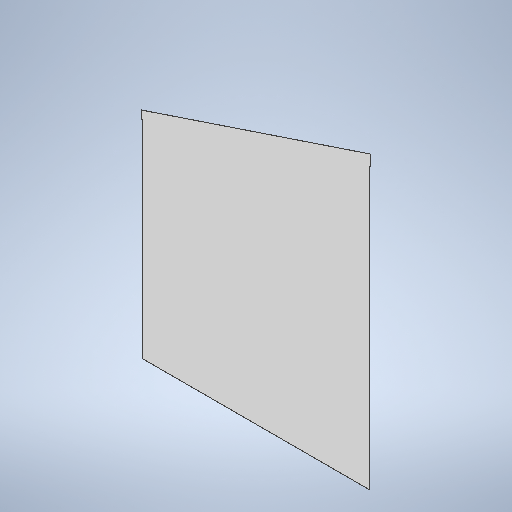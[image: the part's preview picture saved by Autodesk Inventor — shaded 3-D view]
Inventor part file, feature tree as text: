
AUTODESK INVENTOR PART (.ipt)
format: ipt  version: 2025 (Build 290162010, 162A)  size: 226,304 bytes
history: native  units: in
note: dims shown in document units (in); Inventor stores cm internally (conversion verified against a paired STEP export)
features: extrude x1, sketch x1
ambient origin geometry x8: Origin, YZ Plane, XZ Plane, XY Plane, X Axis, Y Axis, Z Axis, Center Point
bodies: Solid1 (feature_tree)
feature tree (2):
  extrude  "Extrusion1"  Depth=0.694in
  sketch  "Sketch1"  dims[d1=121.5in d2=0.694in d3=4.682in d4=133.625in d5=164.773in d6=0.757in d7=6.457in d8=0.0625in d9=0.0in]
